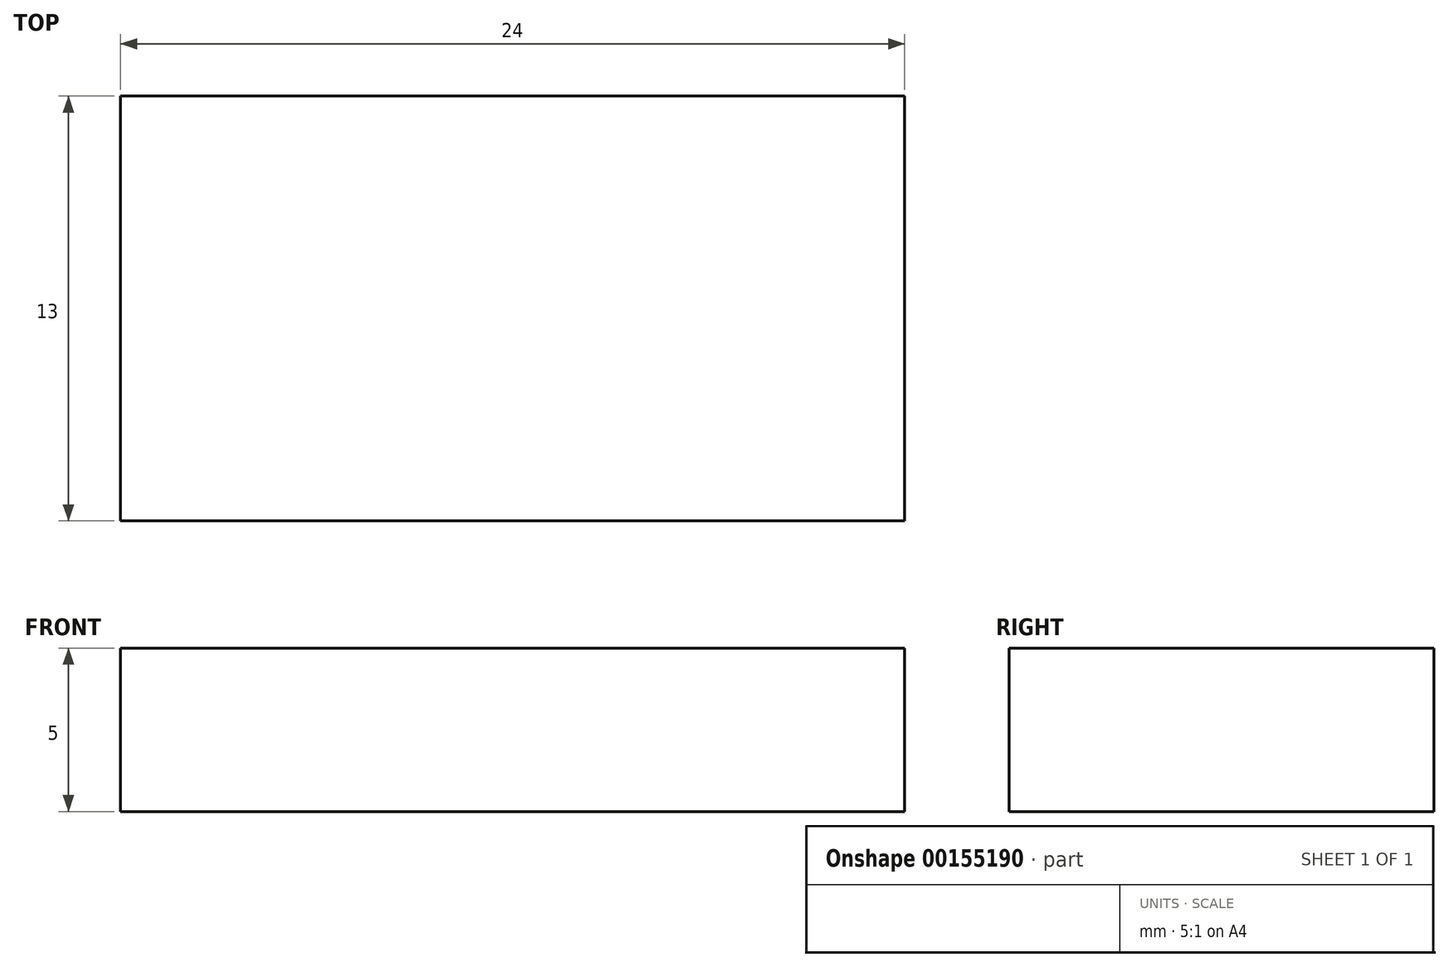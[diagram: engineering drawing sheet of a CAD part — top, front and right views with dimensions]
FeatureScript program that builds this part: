
annotation { "Feature Type Name" : "Feature", "Feature Type Description" : "" }
export const myFeature = defineFeature(function(context is Context, id is Id, definition is map)
    precondition{}
    {
        {
            var Q0;
            Q0=qCreatedBy(makeId("Top.planeOp"),FACE);
            var sketch = newSketch(context, id + "F0", { "sketchPlane" : qUnion([Q0])});
            skLineSegment(sketch, "E0.bottom", {"start": v(12, 6.5) * mm, "end": v(-12, 6.5) * mm});
            skLineSegment(sketch, "E0.top", {"start": v(12, -6.5) * mm, "end": v(-12, -6.5) * mm});
            skLineSegment(sketch, "E0.left", {"start": v(12, 6.5) * mm, "end": v(12, -6.5) * mm});
            skLineSegment(sketch, "E0.right", {"start": v(-12, 6.5) * mm, "end": v(-12, -6.5) * mm});
            skPoint(sketch, "E0.middle", {"position": v(0, 0) * mm});
            skSolve(sketch);
        }
        {
            var Q0;
            Q0=qSketchRegion(id+"F0",true);
            extrude(context, id + "F1", {"entities" : qUnion([Q0]), "endBound" : BoundingType.SYMMETRIC, "depth" : 5 * mm});
        }
    });
